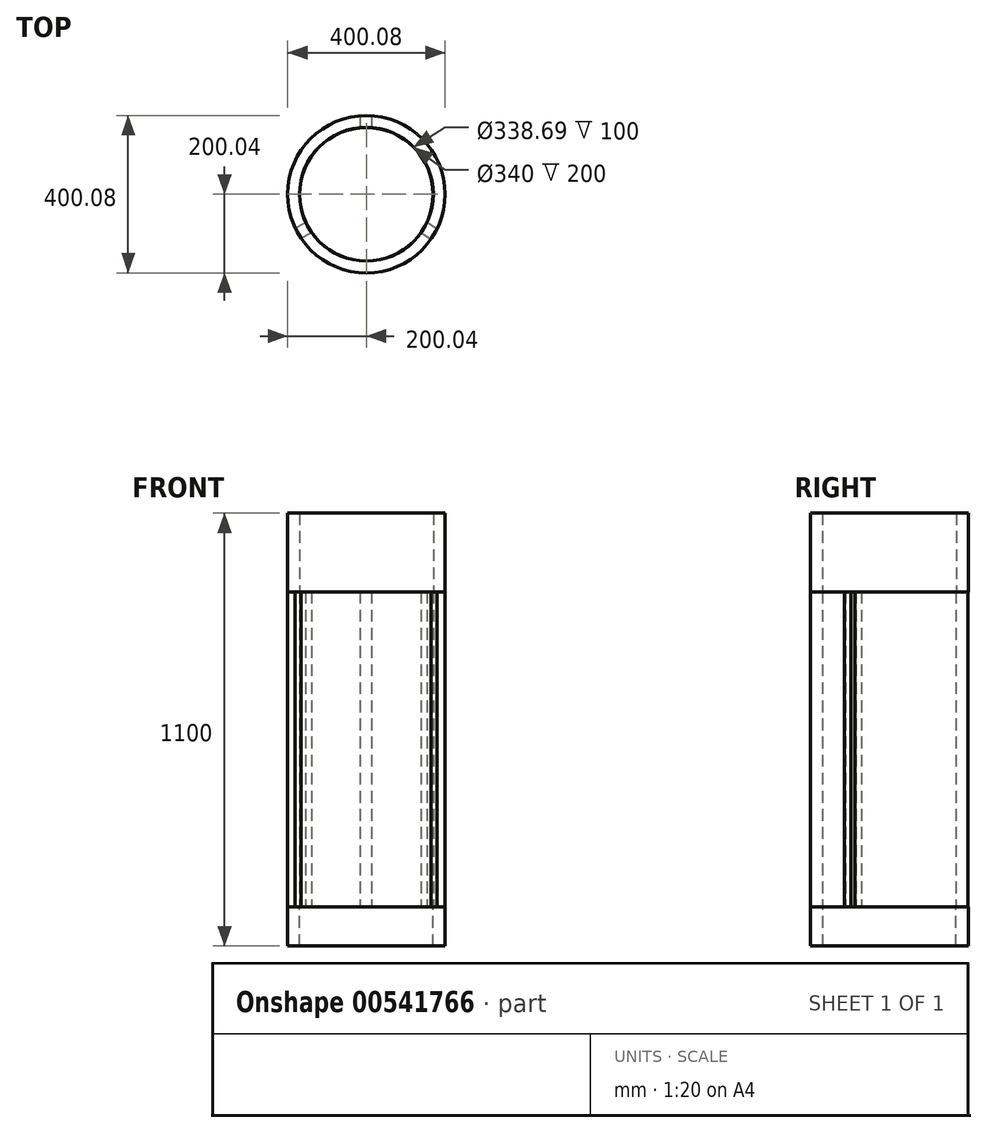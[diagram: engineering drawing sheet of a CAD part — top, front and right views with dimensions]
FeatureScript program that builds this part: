
annotation { "Feature Type Name" : "Feature", "Feature Type Description" : "" }
export const myFeature = defineFeature(function(context is Context, id is Id, definition is map)
    precondition{}
    {
        {
            var Q0;
            Q0=qCreatedBy(makeId("Top.planeOp"),FACE);
            var sketch = newSketch(context, id + "F0", { "sketchPlane" : qUnion([Q0])});
            skArc(sketch, "E0", {"start": v(-16.6, 199.3) * mm, "mid": v(-173.33, 99.78) * mm, "end": v(-180.7, -85.73) * mm});
            skArc(sketch, "E1", {"start": v(-16.6, 169.19) * mm, "mid": v(-147.63, 84.3) * mm, "end": v(-154.14, -71.7) * mm});
            skLineSegment(sketch, "E2", {"start": v(0, 170) * mm, "end": v(0, 200) * mm});
            skLineSegment(sketch, "E3", {"start": v(-147.22, -85) * mm, "end": v(-173.2, -100) * mm});
            skLineSegment(sketch, "E4", {"start": v(147.22, -85) * mm, "end": v(173.2, -100) * mm});
            skPoint(sketch, "E5", {"position": v(160.21, -92.5) * mm});
            skPoint(sketch, "E6", {"position": v(0, 185) * mm});
            skArc(sketch, "E7.trimOffspring", {"start": v(154.35, -71.26) * mm, "mid": v(146.7, 85.9) * mm, "end": v(13.4, 169.47) * mm});
            skArc(sketch, "E8.trimOffspring", {"start": v(179.62, -87.95) * mm, "mid": v(173.14, 100.1) * mm, "end": v(13.4, 199.55) * mm});
            skArc(sketch, "E9.trimOffspring", {"start": v(-139.14, -97.68) * mm, "mid": v(0.24, -170) * mm, "end": v(139.42, -97.28) * mm});
            skArc(sketch, "E10.trimOffspring", {"start": v(-165.84, -111.79) * mm, "mid": v(-1.23, -200) * mm, "end": v(164.45, -113.83) * mm});
            skLineSegment(sketch, "E11", {"start": v(-165.84, -111.79) * mm, "end": v(-139.14, -97.68) * mm});
            skLineSegment(sketch, "E12", {"start": v(-180.7, -85.73) * mm, "end": v(-154.14, -71.7) * mm});
            skLineSegment(sketch, "E13", {"start": v(154.35, -71.26) * mm, "end": v(179.62, -87.95) * mm});
            skLineSegment(sketch, "E14", {"start": v(139.42, -97.28) * mm, "end": v(164.45, -113.83) * mm});
            skLineSegment(sketch, "E15", {"start": v(-16.6, 199.3) * mm, "end": v(-16.6, 169.19) * mm});
            skLineSegment(sketch, "E16", {"start": v(13.4, 199.55) * mm, "end": v(13.4, 169.47) * mm});
            skSolve(sketch);
        }
        {
            var Q0;
            Q0 = qSketchRegion(id + "F0", true);
            extrude(context, id + "F1", {"entities" : qUnion([Q0]), "depth" : 800 * mm, "offsetDistance" : 25 * mm});
        }
        {
            var Q0;
            Q0=makeQuery(id+"F1.opExtrude","CAP_FACE",FACE,{"disambiguationData":[OSD([sQuery(id+"F0.wireOp",EDGE,"E0"),sQuery(id+"F0.wireOp",EDGE,"E1"),sQuery(id+"F0.wireOp",EDGE,"QxE7AbIh-Si8Y-BE0y-LENI-OwJc2kWLV3lR"),sQuery(id+"F0.wireOp",EDGE,"SgfulNmA-KAEL-wRP7-0YFW-wfojbDtQQc0Z")])],"isStart":false});
            var sketch = newSketch(context, id + "F2", { "sketchPlane" : qUnion([Q0])});
            skCircle(sketch, "E17", {"center": v(0, 0) * mm, "radius": 200 * mm});
            skCircle(sketch, "E18", {"center": v(0, 0) * mm, "radius": 170 * mm});
            skSolve(sketch);
        }
        {
            var Q0;
            Q0 = qSketchRegion(id + "F2", true);
            extrude(context, id + "F3", {"entities" : qUnion([Q0]), "depth" : 200 * mm, "offsetDistance" : 25 * mm});
        }
        {
            var Q0;
            Q0=makeQuery(id+"F1.opExtrude","CAP_FACE",FACE,{"disambiguationData":[OSD([sQuery(id+"F0.wireOp",EDGE,"E0"),sQuery(id+"F0.wireOp",EDGE,"E1"),sQuery(id+"F0.wireOp",EDGE,"E12"),sQuery(id+"F0.wireOp",EDGE,"E15")])],"isStart":true});
            var sketch = newSketch(context, id + "F4", { "sketchPlane" : qUnion([Q0])});
            skCircle(sketch, "E19", {"center": v(0, 0) * mm, "radius": 169.34 * mm});
            skCircle(sketch, "E20", {"center": v(0, 0) * mm, "radius": 200.04 * mm});
            skSolve(sketch);
        }
        {
            var Q0;
            Q0 = qSketchRegion(id + "F4", true);
            extrude(context, id + "F5", {"entities" : qUnion([Q0]), "depth" : 100 * mm, "offsetDistance" : 25 * mm});
        }
    });
